FCSTD DOCUMENT  (FreeCAD 0.19.4R1_voidlinux)
Label: asm_main
License: All rights reserved
LicenseURL: http://en.wikipedia.org/wiki/All_rights_reserved
objects: App::DocumentObjectGroup×3, App::Link×2, PartDesign::CoordinateSystem×1, App::FeaturePython×1, App::Part×1
note: 1 computed .brp shape members not serialized (recipe doc carries the construction recipe); baked Part::Feature solids carry a one-line shape summary decoded from their .brp
EXTERNAL_REF file=master_animator.FCStd obj=Variables
EXTERNAL_REF file=asm_front_shell.FCStd obj=Model
EXTERNAL_REF file=asm_back_shell.FCStd obj=LCS_Origin
EXTERNAL_REF file=asm_back_shell.FCStd obj=Model

FEATURE [App::DocumentObjectGroup] Parts
FEATURE [PartDesign::CoordinateSystem] LCS_Origin
  AttacherType = Attacher::AttachEngine3D
  MapMode = 2
  Support = -> [X_Axis]
  expr: .AttachmentOffset.Base.z = -master_animator#Variables.explode * 3
FEATURE [App::DocumentObjectGroup] Constraints
FEATURE [App::FeaturePython] Variables  # WARN: FeaturePython — macro-defined, semantics opaque (R4)
  Type = App::PropertyContainer
FEATURE [App::DocumentObjectGroup] Configurations
FEATURE [App::Link] asm_front_shell
  LinkedObject = -> <external asm_front_shell.FCStd>#Model
FEATURE [App::Link] asm_back_shell
  AttachedBy = #LCS_Origin
  AttachedTo = Parent Assembly#LCS_Origin
  AttachmentOffset = pos=(0,-31.5,-6.5) rot=(0,1,0;3.14159rad)
  LinkPlacement = pos=(0,-31.5,-6.5) rot=(0,1,0;3.14159rad)
  LinkedObject = -> <external asm_back_shell.FCStd>#Model
  Placement = pos=(0,-31.5,-6.5) rot=(0,1,0;3.14159rad)
  SolverId = Asm4EE
  expr: Placement = LCS_Origin.Placement * AttachmentOffset * asm_back_shell#LCS_Origin.Placement ^ -1
FEATURE [App::Part] Model
  AssemblyType = Part::Link
  Group = -> [LCS_Origin,Constraints,Variables,Configurations,asm_front_shell,asm_back_shell]
  Origin = -> Origin
  Type = Assembly

RESOLVED EXTERNAL PARTS (link-assembly join: the EXTERNAL_REF files above that resolve inside this repo's crawl, each included once):
---- part asm_back_shell.FCStd = doc fcstd_10172c3113f3 ----
FCSTD DOCUMENT  (FreeCAD 0.19.4R1_voidlinux)
Label: asm_back_shell
License: All rights reserved
LicenseURL: http://en.wikipedia.org/wiki/All_rights_reserved
objects: App::Link×6, App::DocumentObjectGroup×3, PartDesign::CoordinateSystem×1, App::FeaturePython×1, App::Part×1
note: 1 computed .brp shape members not serialized (recipe doc carries the construction recipe); baked Part::Feature solids carry a one-line shape summary decoded from their .brp
EXTERNAL_REF file=shell_back.FCStd obj=Part
EXTERNAL_REF file=asm_battery_container.FCStd obj=LCS_Origin
EXTERNAL_REF file=asm_battery_container.FCStd obj=Model
EXTERNAL_REF file=asm_wheel.FCStd obj=LCS_Origin
EXTERNAL_REF file=shell_back.FCStd obj=LCS_wheel_rest
EXTERNAL_REF file=asm_wheel.FCStd obj=Model
EXTERNAL_REF file=clock_inner.FCStd obj=LCS_1
EXTERNAL_REF file=clock_inner.FCStd obj=Part
EXTERNAL_REF file=alarm_button.FCStd obj=LCS_bottom_edge
EXTERNAL_REF file=shell_back.FCStd obj=LCS_alarm_button_edge
EXTERNAL_REF file=alarm_button.FCStd obj=Part
EXTERNAL_REF file=asm_back_lid.FCStd obj=LCS_Origin
EXTERNAL_REF file=asm_back_lid.FCStd obj=Model

FEATURE [App::DocumentObjectGroup] Parts
FEATURE [PartDesign::CoordinateSystem] LCS_Origin
  AttacherType = Attacher::AttachEngine3D
  MapMode = 2
  Support = -> [X_Axis]
FEATURE [App::DocumentObjectGroup] Constraints
FEATURE [App::FeaturePython] Variables  # WARN: FeaturePython — macro-defined, semantics opaque (R4)
  Type = App::PropertyContainer
FEATURE [App::DocumentObjectGroup] Configurations
FEATURE [App::Link] battery_body_part
  LinkedObject = -> <external shell_back.FCStd>#Part
FEATURE [App::Link] asm_battery_container
  AttachedBy = #LCS_Origin
  AttachedTo = Parent Assembly#LCS_Origin
  AttachmentOffset = pos=(0,3.6,-4) rot=(0,0,1;0rad)
  LinkPlacement = pos=(0,3.6,-4) rot=(0,0,1;0rad)
  LinkedObject = -> <external asm_battery_container.FCStd>#Model
  Placement = pos=(0,3.6,-4) rot=(0,0,1;0rad)
  SolverId = Asm4EE
  expr: Placement = LCS_Origin.Placement * AttachmentOffset * asm_battery_container#LCS_Origin.Placement ^ -1
FEATURE [App::Link] asm_wheel
  AttachedBy = #LCS_Origin
  AttachedTo = battery_body_part#LCS_wheel_rest
  AttachmentOffset = pos=(0,0,2) rot=(0,0,1;0rad)
  LinkPlacement = pos=(7,38,18) rot=(0,0,1;1.5708rad)
  LinkedObject = -> <external asm_wheel.FCStd>#Model
  Placement = pos=(7,38,18) rot=(0,0,1;1.5708rad)
  SolverId = Asm4EE
  expr: Placement = battery_body_part.Placement * shell_back#LCS_wheel_rest.Placement * AttachmentOffset * asm_wheel#LCS_Origin.Placement ^ -1
FEATURE [App::Link] clock_inner
  AttachedBy = #LCS_1
  AttachedTo = Parent Assembly#LCS_Origin
  AttachmentOffset = pos=(0,39.6,11) rot=(0,0,1;1.5708rad)
  LinkPlacement = pos=(-3e-16,22.1,-4) rot=(0,0,1;0rad)
  LinkedObject = -> <external clock_inner.FCStd>#Part
  Placement = pos=(-3e-16,22.1,-4) rot=(0,0,1;0rad)
  SolverId = Asm4EE
  expr: Placement = LCS_Origin.Placement * AttachmentOffset * clock_inner#LCS_1.Placement ^ -1
FEATURE [App::Link] alarm_button
  AttachedBy = #LCS_bottom_edge
  AttachedTo = battery_body_part#LCS_alarm_button_edge
  AttachmentOffset = pos=(0,0,0) rot=(0.707107,0.707107,0;3.14159rad)
  LinkPlacement = pos=(5.8e-15,63.5,-3.5) rot=(0,0.707107,0.707107;3.14159rad)
  LinkedObject = -> <external alarm_button.FCStd>#Part
  Placement = pos=(5.8e-15,63.5,-3.5) rot=(0,0.707107,0.707107;3.14159rad)
  SolverId = Asm4EE
  expr: Placement = battery_body_part.Placement * shell_back#LCS_alarm_button_edge.Placement * AttachmentOffset * alarm_button#LCS_bottom_edge.Placement ^ -1
FEATURE [App::Link] back_lid_model
  AttachedBy = #LCS_Origin
  AttachedTo = Parent Assembly#LCS_Origin
  AttachmentOffset = pos=(0,0,18) rot=(0,1,0;3.14159rad)
  LinkPlacement = pos=(0,0,18) rot=(0,1,0;3.14159rad)
  LinkedObject = -> <external asm_back_lid.FCStd>#Model
  Placement = pos=(0,0,18) rot=(0,1,0;3.14159rad)
  SolverId = Asm4EE
  expr: Placement = LCS_Origin.Placement * AttachmentOffset * asm_back_lid#LCS_Origin.Placement ^ -1
FEATURE [App::Part] Model
  AssemblyType = Part::Link
  Group = -> [LCS_Origin,Constraints,Variables,Configurations,battery_body_part,asm_battery_container,asm_wheel,clock_inner,alarm_button,back_lid_model]
  Origin = -> Origin
  Type = Assembly
---- part asm_front_shell.FCStd = doc fcstd_74635892c40a ----
FCSTD DOCUMENT  (FreeCAD 0.19.4R1_voidlinux)
Label: asm_front_shell
License: All rights reserved
LicenseURL: http://en.wikipedia.org/wiki/All_rights_reserved
objects: App::DocumentObjectGroup×3, App::Link×3, PartDesign::CoordinateSystem×1, App::FeaturePython×1, App::Part×1
note: 1 computed .brp shape members not serialized (recipe doc carries the construction recipe); baked Part::Feature solids carry a one-line shape summary decoded from their .brp
EXTERNAL_REF file=asm_clock_hands.FCStd obj=LCS_Origin
EXTERNAL_REF file=asm_clock_hands.FCStd obj=Model
EXTERNAL_REF file=shell_front.FCStd obj=LCS_clock_front_face
EXTERNAL_REF file=shell_front.FCStd obj=Part
EXTERNAL_REF file=front_glassv2.FCStd obj=LCS_bottom_face
EXTERNAL_REF file=front_glassv2.FCStd obj=Part

FEATURE [App::DocumentObjectGroup] Parts
FEATURE [PartDesign::CoordinateSystem] LCS_Origin
  AttacherType = Attacher::AttachEngine3D
  MapMode = 2
  Support = -> [X_Axis]
FEATURE [App::DocumentObjectGroup] Constraints
FEATURE [App::FeaturePython] Variables  # WARN: FeaturePython — macro-defined, semantics opaque (R4)
  Type = App::PropertyContainer
FEATURE [App::DocumentObjectGroup] Configurations
FEATURE [App::Link] asm_clock_hands
  AttachedBy = #LCS_Origin
  AttachedTo = Parent Assembly#LCS_Origin
  LinkedObject = -> <external asm_clock_hands.FCStd>#Model
  SolverId = Asm4EE
  expr: Placement = LCS_Origin.Placement * AttachmentOffset * asm_clock_hands#LCS_Origin.Placement ^ -1
FEATURE [App::Link] shell_front
  AttachedBy = #LCS_clock_front_face
  AttachedTo = Parent Assembly#LCS_Origin
  AttachmentOffset = pos=(0,0,0) rot=(0,0,1;1.5708rad)
  LinkPlacement = pos=(7e-16,1.7e-15,9) rot=(0,0,1;0rad)
  LinkedObject = -> <external shell_front.FCStd>#Part
  Placement = pos=(7e-16,1.7e-15,9) rot=(0,0,1;0rad)
  SolverId = Asm4EE
  expr: Placement = LCS_Origin.Placement * AttachmentOffset * shell_front#LCS_clock_front_face.Placement ^ -1
FEATURE [App::Link] front_glass
  AssemblyType = Part::Link
  AttachedBy = #LCS_bottom_face
  AttachedTo = Parent Assembly#LCS_Origin
  AttachmentOffset = pos=(0,0,0) rot=(0,0,1;1.5708rad)
  LinkPlacement = pos=(0.000149151,0.0095018,9) rot=(0,0,1;1e-06rad)
  LinkedObject = -> <external front_glassv2.FCStd>#Part
  Placement = pos=(0.000149151,0.0095018,9) rot=(0,0,1;1e-06rad)
  SolverId = Asm4EE
  expr: Placement = LCS_Origin.Placement * AttachmentOffset * front_glassv2#LCS_bottom_face.Placement ^ -1
FEATURE [App::Part] Model
  Group = -> [LCS_Origin,Constraints,Variables,Configurations,asm_clock_hands,shell_front,front_glass]
  Origin = -> Origin
  Type = Assembly
